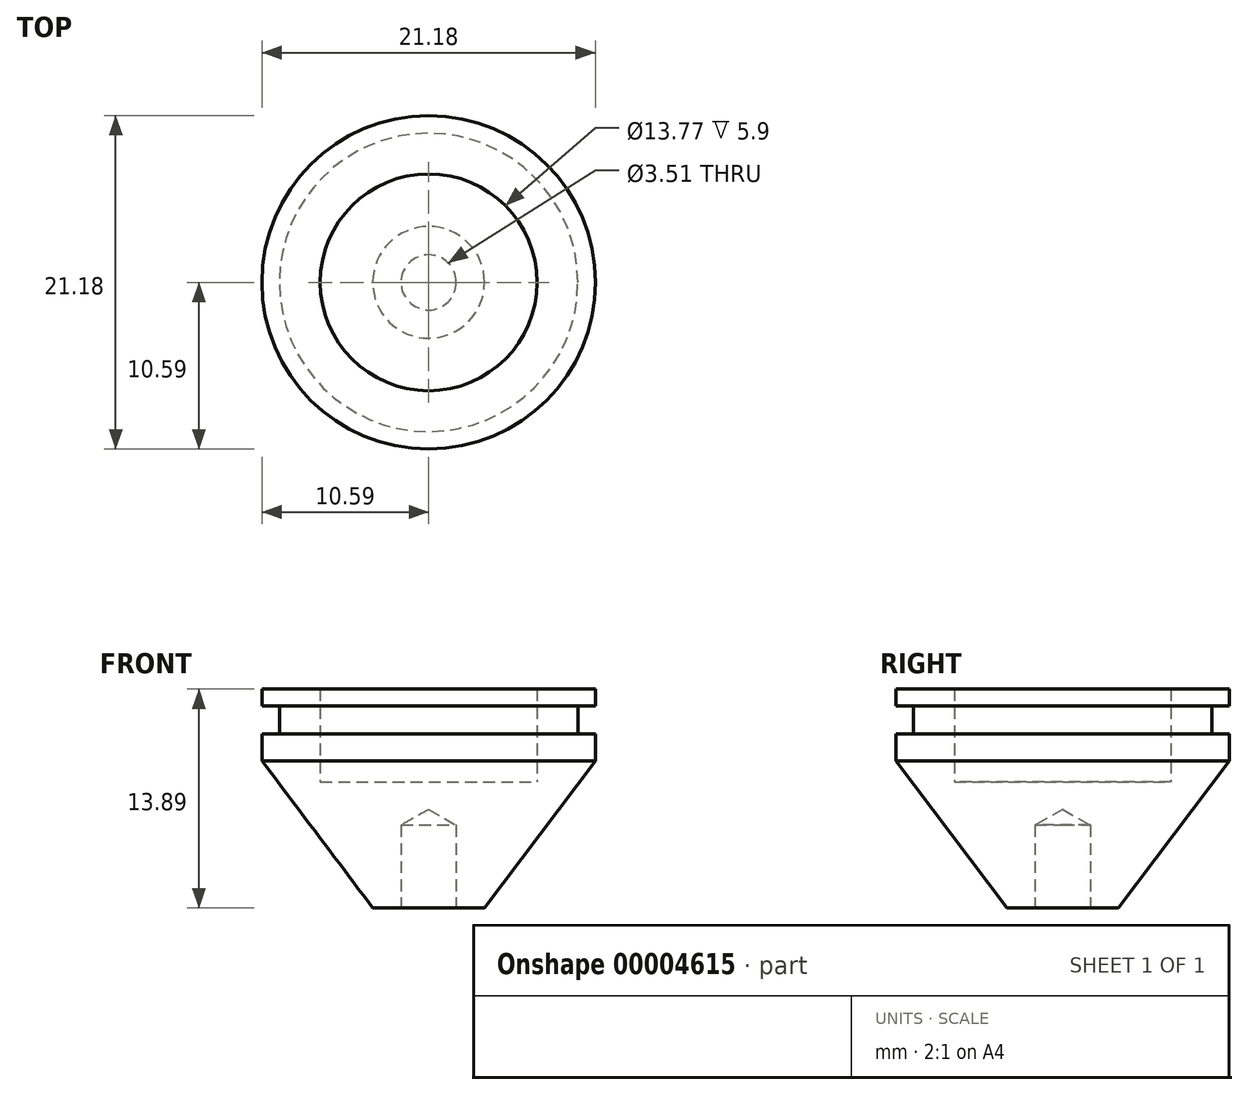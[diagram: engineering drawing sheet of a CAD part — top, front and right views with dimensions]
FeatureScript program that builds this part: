
annotation { "Feature Type Name" : "Feature", "Feature Type Description" : "" }
export const myFeature = defineFeature(function(context is Context, id is Id, definition is map)
    precondition{}
    {
        {
            var Q0;
            Q0=qCreatedBy(makeId("Front.planeOp"),FACE);
            var sketch = newSketch(context, id + "F0", { "sketchPlane" : qUnion([Q0])});
            skLineSegment(sketch, "E0", {"start": v(10.6, 13.89) * mm, "end": v(10.6, 12.81) * mm});
            skLineSegment(sketch, "E1", {"start": v(10.6, 12.81) * mm, "end": v(9.47, 12.81) * mm});
            skLineSegment(sketch, "E2", {"start": v(9.47, 12.81) * mm, "end": v(9.47, 11.03) * mm});
            skLineSegment(sketch, "E3", {"start": v(9.47, 11.03) * mm, "end": v(10.6, 11.03) * mm});
            skLineSegment(sketch, "E4", {"start": v(10.6, 11.03) * mm, "end": v(10.6, 9.34) * mm});
            skLineSegment(sketch, "E5", {"start": v(10.6, 13.89) * mm, "end": v(6.89, 13.89) * mm});
            skLineSegment(sketch, "E6", {"start": v(6.89, 13.89) * mm, "end": v(6.89, 7.99) * mm});
            skLineSegment(sketch, "E7", {"start": v(10.6, 9.34) * mm, "end": v(3.55, 0) * mm});
            skLineSegment(sketch, "E8", {"start": v(6.89, 7.99) * mm, "end": v(0, 7.99) * mm});
            skLineSegment(sketch, "E9", {"start": v(3.55, 0) * mm, "end": v(1.75, 0) * mm});
            skLineSegment(sketch, "E10", {"start": v(1.75, 0) * mm, "end": v(1.75, 5.26) * mm});
            skLineSegment(sketch, "E11", {"start": v(1.75, 5.26) * mm, "end": v(0, 6.25) * mm});
            skLineSegment(sketch, "E12", {"start": v(0, 6.25) * mm, "end": v(0, 7.99) * mm});
            skLineSegment(sketch, "E13", {"start": v(10.72, 13.9) * mm, "end": v(10.72, 9.4) * mm, "construction": true});
            skSolve(sketch);
        }
        {
            var Q0;
            Q0 = qSketchRegion(id + "F0", true);
            var Q1;
            Q1=sQuery(id+"F0.wireOp",EDGE,"E12");
            revolve(context, id + "F1", {"entities" : qUnion([Q0]), "axis" : qUnion([Q1]), "revolveType" : RevolveType.FULL});
        }
    });
